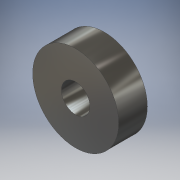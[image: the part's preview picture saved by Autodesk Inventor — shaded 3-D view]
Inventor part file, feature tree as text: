
AUTODESK INVENTOR PART (.ipt)
format: ipt  version: 2016 (Build 200138000, 138)  size: 100,864 bytes
history: native  units: in
note: dims shown in document units (in); Inventor stores cm internally (conversion verified against a paired STEP export)
features: extrude x1, sketch x1
ambient origin geometry x8: Origin, YZ Plane, XZ Plane, XY Plane, X Axis, Y Axis, Z Axis, Center Point
bodies: Solid1 (feature_tree)
feature tree (2):
  extrude  "Extrusion1"  Depth=0.375in
  sketch  "Sketch1"  dims[d0=1.125in d1=0.375in d2=0.375in d3=0.0in]
